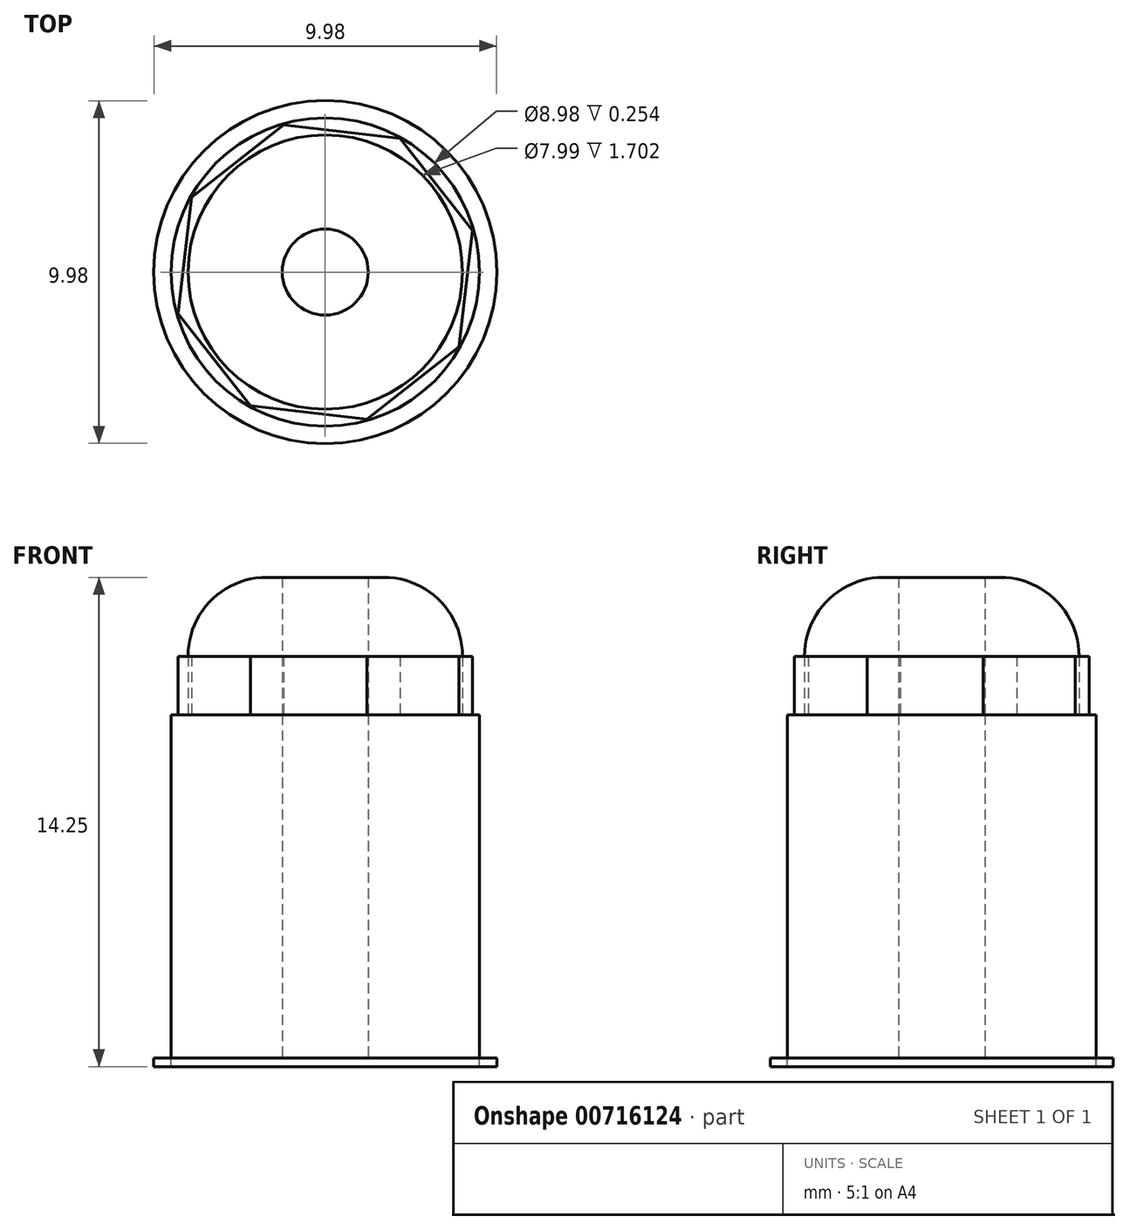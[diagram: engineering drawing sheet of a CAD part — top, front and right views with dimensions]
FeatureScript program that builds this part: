
annotation { "Feature Type Name" : "Feature", "Feature Type Description" : "" }
export const myFeature = defineFeature(function(context is Context, id is Id, definition is map)
    precondition{}
    {
        {
            var Q0;
            Q0=qCreatedBy(makeId("Top.planeOp"),FACE);
            var sketch = newSketch(context, id + "F0", { "sketchPlane" : qUnion([Q0])});
            skCircle(sketch, "E0", {"center": v(0, 0) * mm, "radius": 4.5 * mm});
            skCircle(sketch, "E1", {"center": v(0, 0) * mm, "radius": 1.25 * mm});
            skCircle(sketch, "E2", {"center": v(0, 0) * mm, "radius": 5 * mm});
            skSolve(sketch);
        }
        {
            var Q0;
            Q0=makeQuery(id+"F0.imprint","IMPRINT",FACE,{"disambiguationData":[TD([[makeQuery(id+"F0.imprint","IMPRINT",EDGE,{"derivedFrom":sQuery(id+"F0.wireOp",EDGE,"E0")}),1.0]])]});
            extrude(context, id + "F1", {"entities" : qUnion([Q0]), "depth" : 10 * mm, "offsetDistance" : 25.4 * mm});
        }
        {
            var Q0;
            Q0=makeQuery(id+"F0.imprint","IMPRINT",FACE,{"disambiguationData":[TD([[makeQuery(id+"F0.imprint","IMPRINT",EDGE,{"derivedFrom":sQuery(id+"F0.wireOp",EDGE,"E0")}),-1.0]])]});
            extrude(context, id + "F2", {"entities" : qUnion([Q0]), "operationType" : NewBodyOperationType.ADD, "oppositeDirection" : true, "depth" : 0.25 * mm, "offsetDistance" : 25.4 * mm});
        }
        {
            var Q0;
            Q0=makeQuery(id+"F1.opExtrude","CAP_FACE",FACE,{"disambiguationData":[OSD([sQuery(id+"F0.wireOp",EDGE,"E0"),sQuery(id+"F0.wireOp",EDGE,"E1")])],"isStart":false});
            var sketch = newSketch(context, id + "F3", { "sketchPlane" : qUnion([Q0])});
            skCircle(sketch, "E3", {"center": v(0, 0) * mm, "radius": 4 * mm});
            skCircle(sketch, "E4", {"center": v(0, 0) * mm, "radius": 4.46 * mm});
            skCircle(sketch, "E5.cCircle", {"center": v(0, 0) * mm, "radius": 4.46 * mm, "construction": true});
            skLineSegment(sketch, "E5.0", {"start": v(-4.3, -1.21) * mm, "end": v(-3.89, 2.18) * mm});
            skLineSegment(sketch, "E5.1", {"start": v(-3.89, 2.18) * mm, "end": v(-1.21, 4.3) * mm});
            skLineSegment(sketch, "E5.2", {"start": v(-1.21, 4.3) * mm, "end": v(2.18, 3.89) * mm});
            skLineSegment(sketch, "E5.3", {"start": v(2.18, 3.89) * mm, "end": v(4.3, 1.21) * mm});
            skLineSegment(sketch, "E5.4", {"start": v(4.3, 1.21) * mm, "end": v(3.89, -2.18) * mm});
            skLineSegment(sketch, "E5.5", {"start": v(3.89, -2.18) * mm, "end": v(1.21, -4.3) * mm});
            skLineSegment(sketch, "E5.6", {"start": v(1.21, -4.3) * mm, "end": v(-2.18, -3.89) * mm});
            skLineSegment(sketch, "E5.7", {"start": v(-2.18, -3.89) * mm, "end": v(-4.3, -1.21) * mm});
            skSolve(sketch);
        }
        {
            var Q0;
            Q0=makeQuery(id+"F3.imprint","IMPRINT",FACE,{"disambiguationData":[TD([[makeQuery(id+"F3.imprint","IMPRINT",EDGE,{"derivedFrom":sQuery(id+"F3.wireOp",EDGE,"E3")}),1.0]])]});
            extrude(context, id + "F4", {"entities" : qUnion([Q0]), "depth" : 4 * mm, "offsetDistance" : 25.4 * mm});
        }
        {
            var Q0;
            Q0=makeQuery(id+"F4.opExtrude","CAP_EDGE",EDGE,{"disambiguationData":[OSD([sQuery(id+"F3.wireOp",EDGE,"E3")])],"isStart":false});
            fillet(context, id + "F5", {"entities" : qUnion([Q0]), "radius" : 2.3 * mm, "tangentPropagation" : true, "allowEdgeOverflow" : false});
        }
        {
            var Q0;
            Q0=makeQuery(id+"F3.imprint","IMPRINT",FACE,{"disambiguationData":[TD([[makeQuery(id+"F3.imprint","IMPRINT",EDGE,{"derivedFrom":sQuery(id+"F3.wireOp",EDGE,"E3")}),-1.0]])]});
            extrude(context, id + "F6", {"entities" : qUnion([Q0]), "depth" : 1.7 * mm, "offsetDistance" : 25.4 * mm});
        }
    });
